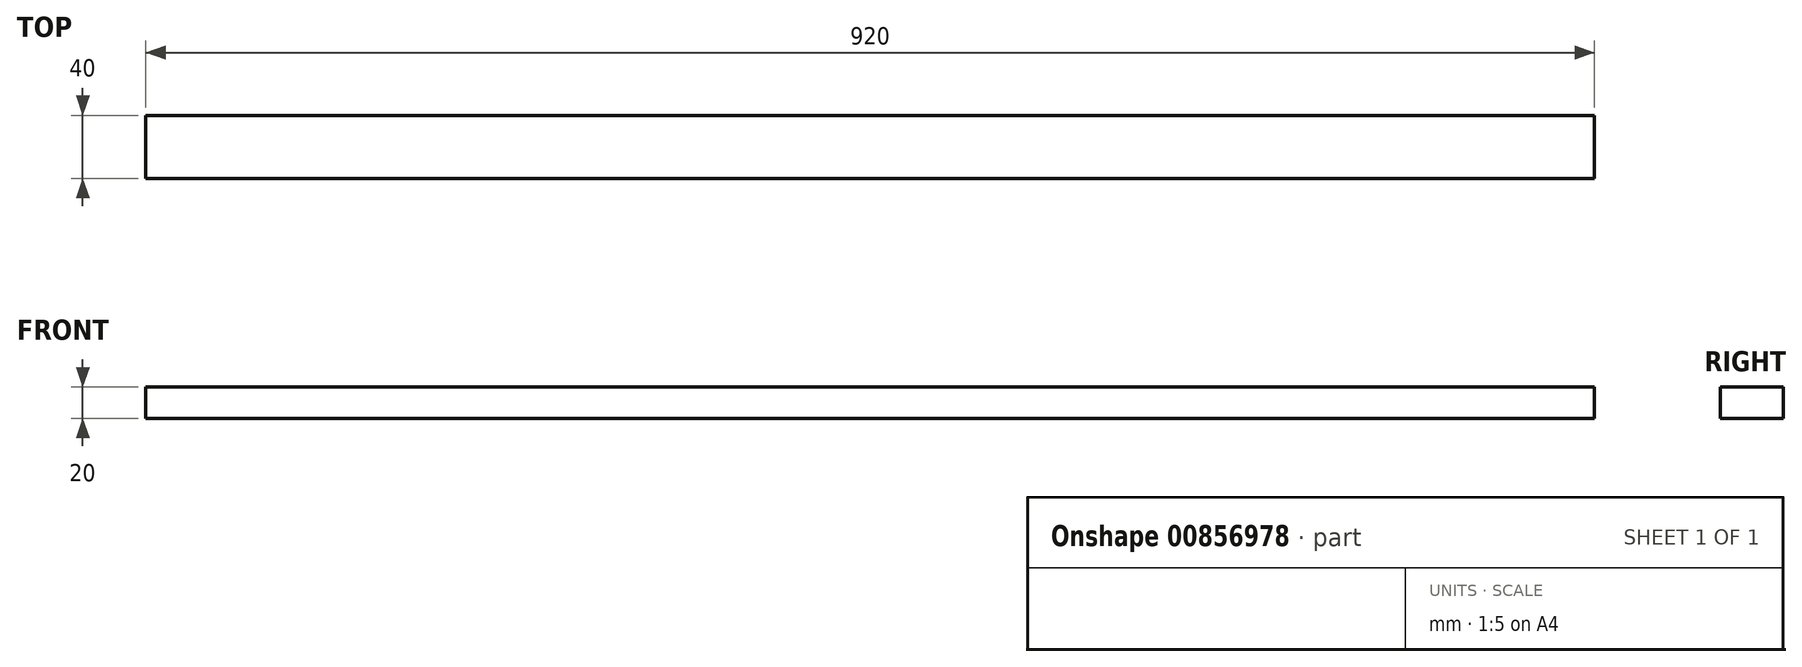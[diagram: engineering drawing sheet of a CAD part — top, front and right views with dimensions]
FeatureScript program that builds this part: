
annotation { "Feature Type Name" : "Feature", "Feature Type Description" : "" }
export const myFeature = defineFeature(function(context is Context, id is Id, definition is map)
    precondition{}
    {
        {
            var Q0;
            Q0=qCreatedBy(makeId("Right.planeOp"),FACE);
            var sketch = newSketch(context, id + "F0", { "sketchPlane" : qUnion([Q0])});
            skLineSegment(sketch, "E0.bottom", {"start": v(0, 0) * mm, "end": v(40, 0) * mm});
            skLineSegment(sketch, "E0.top", {"start": v(0, -20) * mm, "end": v(40, -20) * mm});
            skLineSegment(sketch, "E0.left", {"start": v(0, 0) * mm, "end": v(0, -20) * mm});
            skLineSegment(sketch, "E0.right", {"start": v(40, 0) * mm, "end": v(40, -20) * mm});
            skSolve(sketch);
        }
        {
            var Q0;
            Q0=makeQuery(id+"F0.imprint","IMPRINT",FACE,{"disambiguationData":[TD([[makeQuery(id+"F0.imprint","IMPRINT",EDGE,{"derivedFrom":sQuery(id+"F0.wireOp",EDGE,"E0.bottom")}),-1.0]])]});
            extrude(context, id + "F1", {"entities" : qUnion([Q0]), "depth" : 920 * mm, "offsetDistance" : 25 * mm});
        }
        {
            var Q0;
            Q0=makeQuery(id+"F1.opExtrude","SWEPT_FACE",FACE,{"disambiguationData":[OSD([sQuery(id+"F0.wireOp",EDGE,"E0.right")])]});
            var sketch = newSketch(context, id + "F2", { "sketchPlane" : qUnion([Q0])});
            skLineSegment(sketch, "E1", {"start": v(0, -10) * mm, "end": v(-20, -10) * mm, "construction": true});
            skLineSegment(sketch, "E2", {"start": v(-920, -10) * mm, "end": v(-900, -10) * mm, "construction": true});
            skSolve(sketch);
        }
        {
            var Q0;
            Q0=makeQuery(id+"F1.opExtrude","SWEPT_FACE",FACE,{"disambiguationData":[OSD([sQuery(id+"F0.wireOp",EDGE,"E0.left")])]});
            var sketch = newSketch(context, id + "F3", { "sketchPlane" : qUnion([Q0])});
            skLineSegment(sketch, "E3", {"start": v(0, -10) * mm, "end": v(20, -10) * mm, "construction": true});
            skLineSegment(sketch, "E4", {"start": v(920, -10) * mm, "end": v(900, -10) * mm, "construction": true});
            skSolve(sketch);
        }
    });
